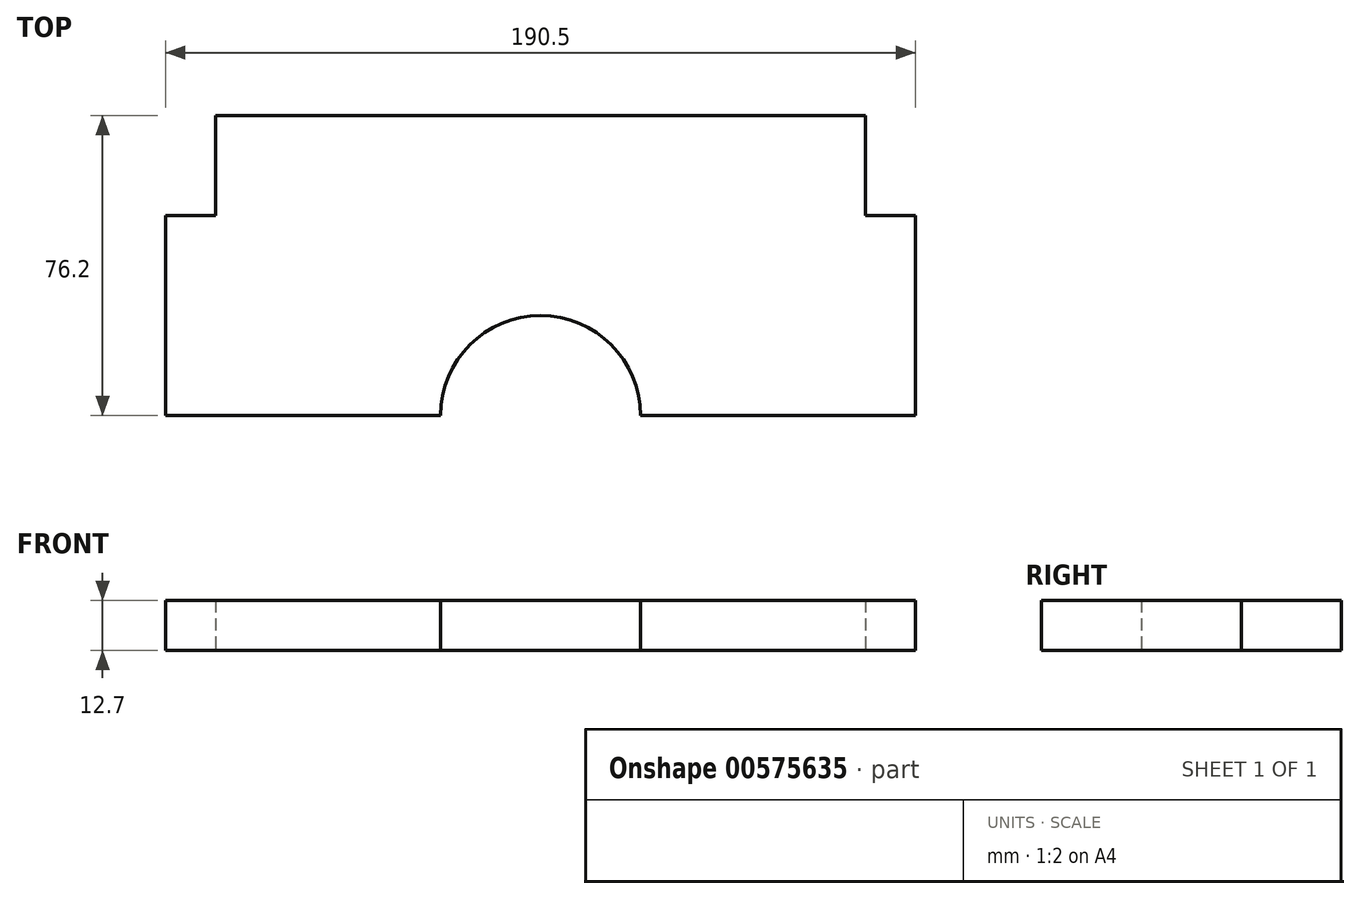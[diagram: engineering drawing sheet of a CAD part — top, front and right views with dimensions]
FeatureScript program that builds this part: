
annotation { "Feature Type Name" : "Feature", "Feature Type Description" : "" }
export const myFeature = defineFeature(function(context is Context, id is Id, definition is map)
    precondition{}
    {
        {
            var Q0;
            Q0=qCreatedBy(makeId("Top.planeOp"),FACE);
            var sketch = newSketch(context, id + "F0", { "sketchPlane" : qUnion([Q0])});
            skLineSegment(sketch, "E0.bottom", {"start": v(-110.46, 25.4) * mm, "end": v(54.64, 25.4) * mm});
            skLineSegment(sketch, "E0.top", {"start": v(-110.46, -50.8) * mm, "end": v(-53.31, -50.8) * mm});
            skLineSegment(sketch, "E0.left", {"start": v(-110.46, 25.4) * mm, "end": v(-110.46, -50.8) * mm});
            skLineSegment(sketch, "E0.right", {"start": v(54.64, 25.4) * mm, "end": v(54.64, -50.8) * mm});
            skLineSegment(sketch, "E1.bottom", {"start": v(54.64, -50.8) * mm, "end": v(67.34, -50.8) * mm});
            skLineSegment(sketch, "E1.top", {"start": v(54.64, 0) * mm, "end": v(67.34, 0) * mm});
            skLineSegment(sketch, "E1.left", {"start": v(54.64, -50.8) * mm, "end": v(54.64, 0) * mm});
            skLineSegment(sketch, "E1.right", {"start": v(67.34, -50.8) * mm, "end": v(67.34, 0) * mm});
            skLineSegment(sketch, "E2.bottom", {"start": v(-110.46, -50.8) * mm, "end": v(-123.16, -50.8) * mm});
            skLineSegment(sketch, "E2.top", {"start": v(-110.46, 0) * mm, "end": v(-123.16, 0) * mm});
            skLineSegment(sketch, "E2.left", {"start": v(-110.46, -50.8) * mm, "end": v(-110.46, 0) * mm});
            skLineSegment(sketch, "E2.right", {"start": v(-123.16, -50.8) * mm, "end": v(-123.16, 0) * mm});
            skArc(sketch, "E3", {"start": v(-2.51, -50.8) * mm, "mid": v(-27.91, -25.4) * mm, "end": v(-53.31, -50.8) * mm});
            skLineSegment(sketch, "E4.trimOffspring", {"start": v(-2.51, -50.8) * mm, "end": v(54.64, -50.8) * mm});
            skSolve(sketch);
        }
        {
            var Q0;
            Q0=qSketchRegion(id+"F0",true);
            extrude(context, id + "F1", {"entities" : qUnion([Q0]), "depth" : 12.7 * mm, "offsetDistance" : 25.4 * mm});
        }
    });
